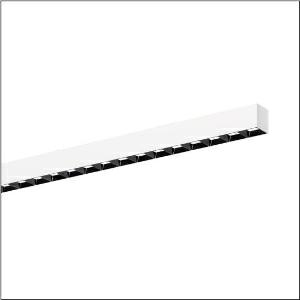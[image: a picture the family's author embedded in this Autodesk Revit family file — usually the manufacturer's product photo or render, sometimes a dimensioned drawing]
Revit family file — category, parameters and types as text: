
# Revit family: silica_r__21_51mx21da44wb_a3a2
name_source: partatom
category: Lighting Fixtures
units: mm (PartAtom-declared; Revit-internal decimal feet)

## family parameters
Cut with Voids When Loaded = No
Host = Face
Light Source = No
Part Type = Normal
Room Calculation Point = No
Round Connector Dimension = Use Diameter
Shared = No

## types (1)
- --- (1 x LED, 4320 lm, 25.6 W, 4000K)
    Apparent Load = 26 VA
    CIE Flux Codes = 87 99 100 100 100
    Color Rendering = 80
    Color Temperature = 4000K
    Default Elevation = 1800 mm
    Description = Silica® 21, office luminaire, primary light control with darklight reflector, of PMMA, black, CAT 2 (L<= 3000cd/m²), light emission: direct distribution, primary light characteristic: symmetric, installation type: surface-mounted, LED, rated luminous flux: 4.320lm, luminous efficacy: 169lm/W, light colour: 840, colour temperature: 4000K, with terminal, 3+2-pole, max. 2.5mm², mains connection: 220..240V, AC, 50/60Hz, rated input power: 25.6W, luminaire housing, of aluminium, traffic white (RAL 9016), length: 1.204mm, width: 53mm, height: 53mm, protection rating (complete): IP20, insulation class (complete): insulation class I (protective earthing), certification: CE, permissible operating ambient temperature: 0..+35°C, standard: EN 50419, packaging unit: 1 piece
    Height = 0 mm  [stored 0 ft]
    Lamp = 1 x LED
    Lamp Light Flux = 4320 lm
    Lamp Power = 25.6 W
    Lamp count = 1
    Length = 1204 mm
    Luminous efficacy = 169 lm/W
    Manufacturer = Siteco
    ModVariant = No
    Model = 51MX21DA44WB
    Mounting Place = Ceiling
    Mounting Type = Recessed
    Number of Poles = 1
    OnlyDefault = Yes
    Power Factor = 1
    Product Name = Silica® 21
    Product group = office luminaire | ceiling recessed
    ProductGroupID = 400
    Protection Class = Protection class I
    Protection Degree = IP 20
    RLX_Detail_Level = 1
    RLX_Emergency_Light_Flux = 0 lm
    RLX_Emergency_Type = 0
    RLX_Emergency_Type_DB = No
    RlxData = <blob elided: 41237 chars, md5=bfbccb1c>
    Socket = socket
    Standby Power = 0 W
    System Light Flux = 4320 lm
    System Power = 26 W
    Type Comments = factory setting: luminous flux: 100 % | dim-lin: 254 | 367 mA
    Type Image = l_1335873.jpg
    URL = http://relux.com
    VarID = @adj_093797
    Voltage = 0 V
    Weight = 0.00 kg
    Width = 53 mm

note: [stored X ft] marks values corroborated as IEEE doubles in the binary element streams (Revit-internal decimal feet)

## geometry (parser evidence)
native form markers: Blend x4, Sweep x10
no freeform markers — native parametric forms only
